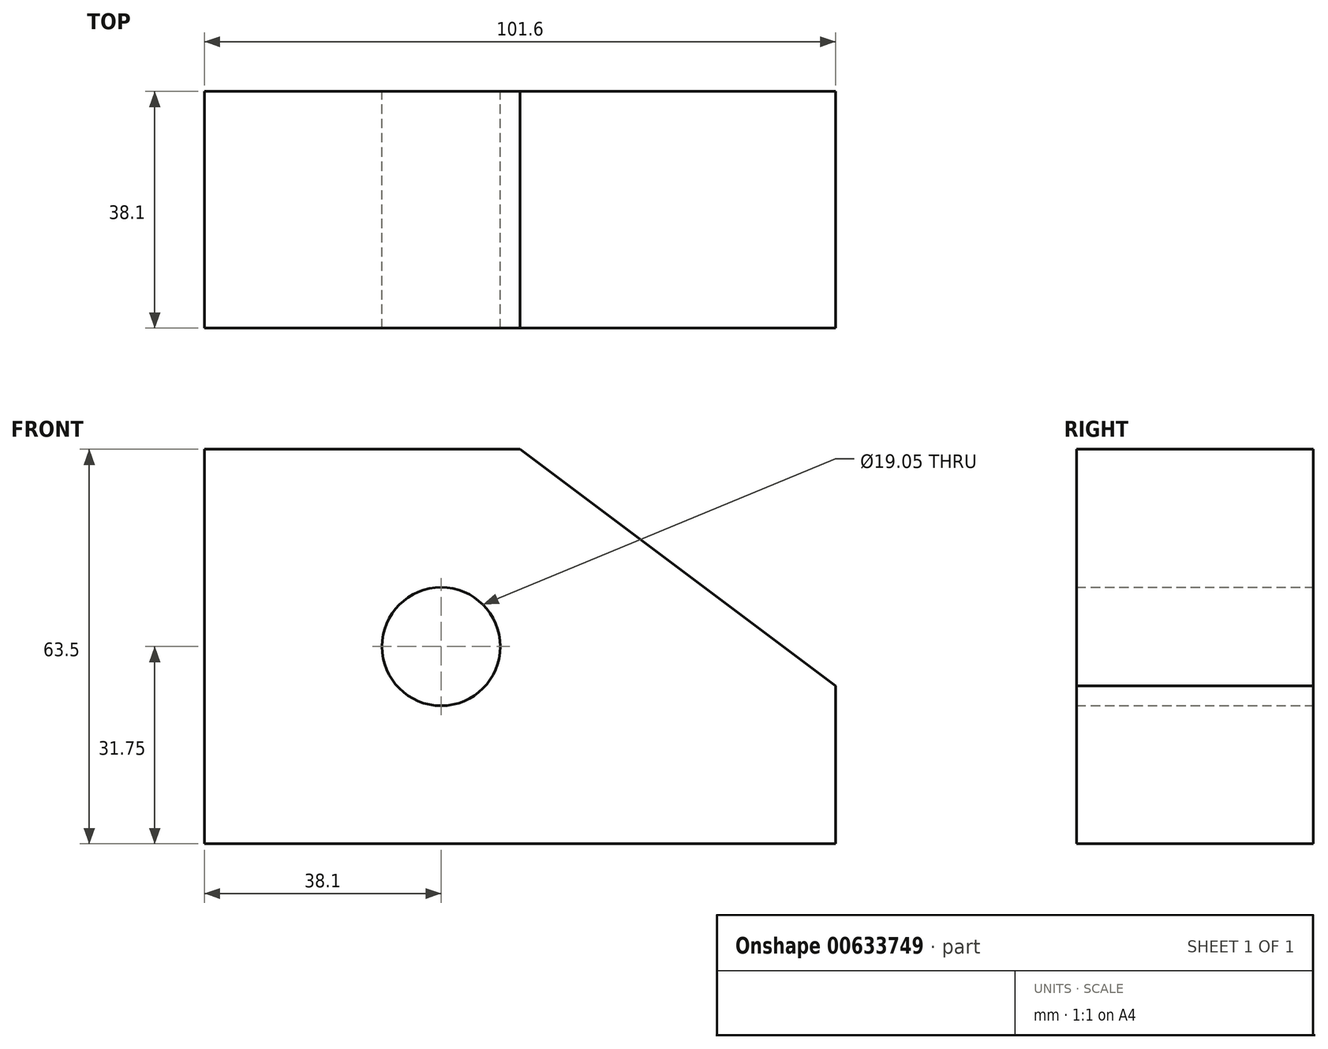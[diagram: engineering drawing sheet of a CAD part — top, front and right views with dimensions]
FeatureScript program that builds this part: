
annotation { "Feature Type Name" : "Feature", "Feature Type Description" : "" }
export const myFeature = defineFeature(function(context is Context, id is Id, definition is map)
    precondition{}
    {
        {
            var Q0;
            Q0=qCreatedBy(makeId("Front.planeOp"),FACE);
            var sketch = newSketch(context, id + "F0", { "sketchPlane" : qUnion([Q0])});
            skLineSegment(sketch, "E0", {"start": v(0, 0) * mm, "end": v(101.6, 0) * mm});
            skLineSegment(sketch, "E1", {"start": v(0, 0) * mm, "end": v(0, 63.5) * mm});
            skLineSegment(sketch, "E2", {"start": v(0, 63.5) * mm, "end": v(50.8, 63.5) * mm});
            skLineSegment(sketch, "E3", {"start": v(101.6, 0) * mm, "end": v(101.6, 25.4) * mm});
            skCircle(sketch, "E4", {"center": v(38.1, 31.75) * mm, "radius": 9.53 * mm});
            skLineSegment(sketch, "E5", {"start": v(50.8, 63.5) * mm, "end": v(101.6, 25.4) * mm});
            skSolve(sketch);
        }
        {
            var Q0;
            Q0=makeQuery(id+"F0.imprint","IMPRINT",FACE,{"disambiguationData":[TD([[makeQuery(id+"F0.imprint","IMPRINT",EDGE,{"derivedFrom":sQuery(id+"F0.wireOp",EDGE,"E0")}),1.0]])]});
            extrude(context, id + "F1", {"entities" : qUnion([Q0]), "depth" : 38.1 * mm, "offsetDistance" : 25.4 * mm});
        }
    });
